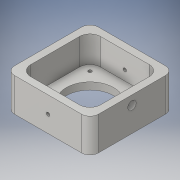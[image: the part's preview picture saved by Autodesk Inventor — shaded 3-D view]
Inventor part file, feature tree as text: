
AUTODESK INVENTOR PART (.ipt)
format: ipt  version: 2016 (Build 200138000, 138)  size: 198,144 bytes
history: native  units: in
note: dims shown in document units (in); Inventor stores cm internally (conversion verified against a paired STEP export)
features: sketch x6, extrude x4, fillet x2, projected_geometry x2, plane x1, hole x1, other x1
ambient origin geometry x8: Origin, YZ Plane, XZ Plane, XY Plane, X Axis, Y Axis, Z Axis, Center Point
bodies: Body1 (feature_tree)
feature tree (17):
  extrude  "Extrusion2"  Depth=2.5in
  fillet  "Fillet1"  Radius=1.0in
  extrude  "Extrusion3"  Depth=0.21in
  plane  "Work Plane1"
  fillet  "Fillet2"  Radius=0.79in
  sketch  "Sketch6"  dims[d29=90.0deg d30=0.3125in]
  hole  "Hole3"  [1 undecoded]
  sketch  "Sketch8"  dims[d31=0.1in d32=0.5in]
  extrude  "Extrusion6"  Depth=0.5in
  extrude  "Extrusion7"  Depth=1.0in TaperAngle=0.0deg
  sketch  "Sketch2"  dims[d3=2.5in d4=2.5in d5=1.0in d6=0.0in]
  sketch  "Sketch3"  dims[d7=0.25in d8=0.21in d9=0.79in d10=0.0in]
  projected_geometry  "Projected Loop1"
  other  "Work Axis1"
  projected_geometry  "Projected Loop4"
  sketch  "Sketch9"  dims[d33=1.0in]
  sketch  "Sketch10"  dims[d46=0.1in d47=0.75in d48=0.375in d49=0.25in d50=0.5635in d51=3.0in d52=0.8108in d53=0.1in d54=0.15in d55=0.15in d56=0.1in d57=0.15in d58=0.15in d59=1.0in d60=0.0in d61=0.25in d62=0.25in d63=0.0in]
note: 1 required parameter value undecoded (feature->parameter linkage not recoverable at this tier; creation-order binding heuristic only, values carry confidence <= 0.55)
